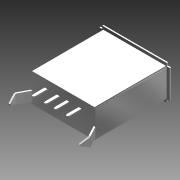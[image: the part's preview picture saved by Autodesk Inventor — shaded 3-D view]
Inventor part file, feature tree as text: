
AUTODESK INVENTOR PART (.ipt)
format: ipt  version: 2011 (Build 150239000, 239)  size: 171,008 bytes
history: native  units: in
note: dims shown in document units (in); Inventor stores cm internally (conversion verified against a paired STEP export)
features: mirror x1, imported_body x1
ambient origin geometry x8: Origin, YZ Plane, XZ Plane, XY Plane, X Axis, Y Axis, Z Axis, Center Point
feature tree (2):
  mirror  "Mirror2"
  imported_body  "Base1"
